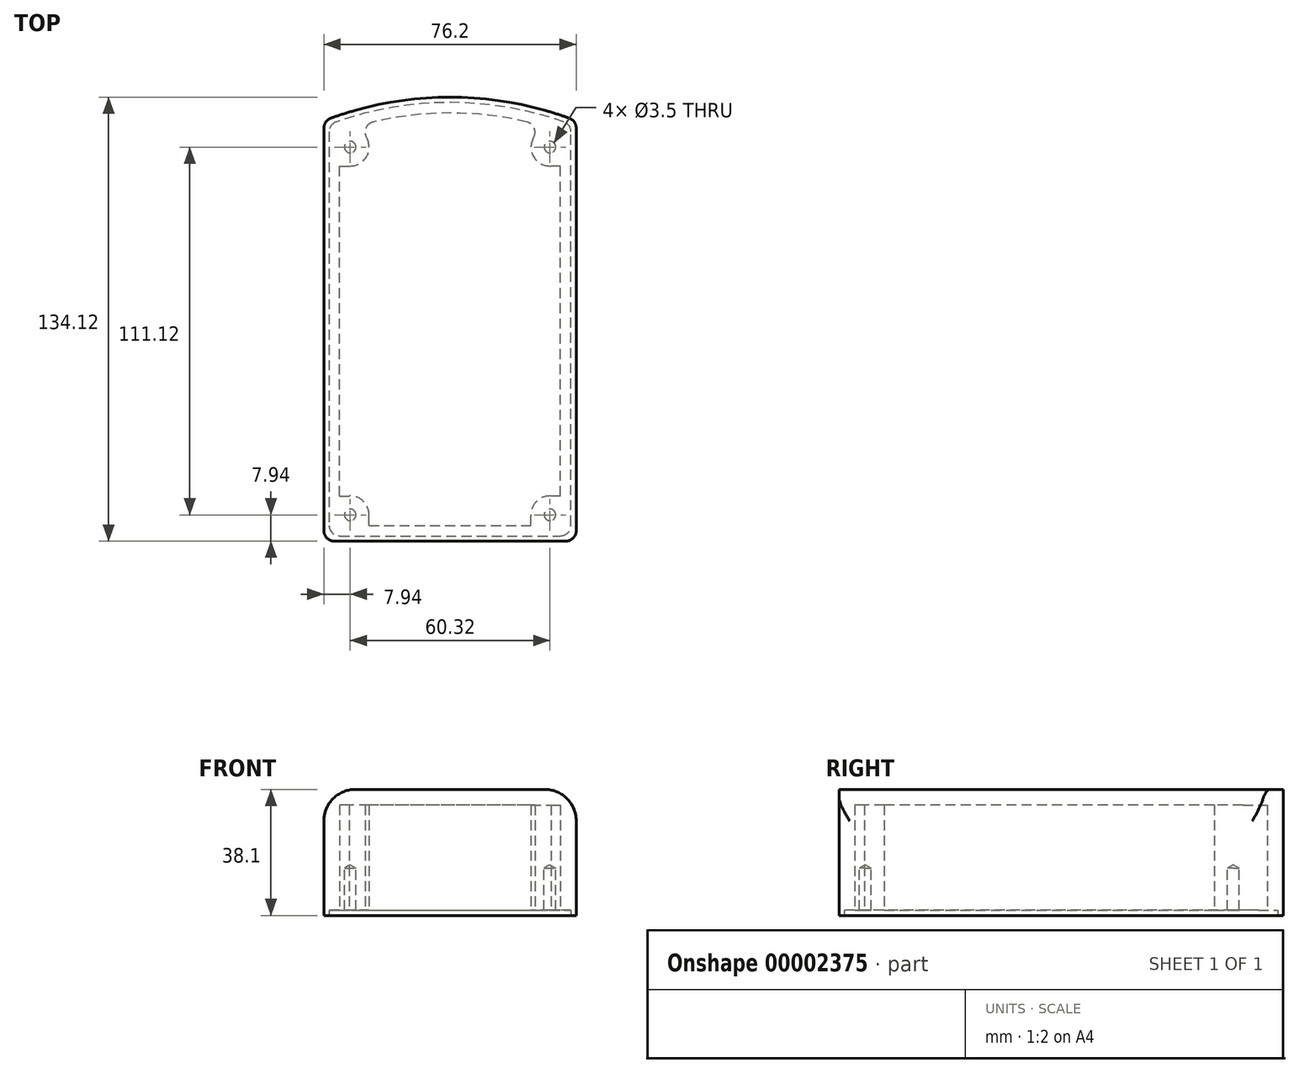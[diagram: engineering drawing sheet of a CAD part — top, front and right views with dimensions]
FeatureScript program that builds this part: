
annotation { "Feature Type Name" : "Feature", "Feature Type Description" : "" }
export const myFeature = defineFeature(function(context is Context, id is Id, definition is map)
    precondition{}
    {
        {
            var Q0;
            Q0=qCreatedBy(makeId("Top.planeOp"),FACE);
            var sketch = newSketch(context, id + "F0", { "sketchPlane" : qUnion([Q0])});
            skLineSegment(sketch, "E0.rect.bottom", {"start": v(38.1, 63.5) * mm, "end": v(-38.1, 63.5) * mm, "construction": true});
            skLineSegment(sketch, "E0.rect.top", {"start": v(38.1, -63.5) * mm, "end": v(-38.1, -63.5) * mm});
            skLineSegment(sketch, "E0.rect.left", {"start": v(38.1, 63.5) * mm, "end": v(38.1, -63.5) * mm});
            skLineSegment(sketch, "E0.rect.right", {"start": v(-38.1, 63.5) * mm, "end": v(-38.1, -63.5) * mm});
            skPoint(sketch, "E0.rect.middle", {"position": v(0, 0) * mm});
            skArc(sketch, "E1", {"start": v(38.1, 63.5) * mm, "mid": v(0, 70.62) * mm, "end": v(-38.1, 63.5) * mm});
            skSolve(sketch);
        }
        {
            var Q0;
            Q0 = qSketchRegion(id + "F0", true);
            extrude(context, id + "F1", {"entities" : qUnion([Q0]), "depth" : 38.1 * mm});
        }
        {
            var Q0;
            Q0=makeQuery(id+"F1.opExtrude","CAP_FACE",FACE,{"disambiguationData":[OSD([sQuery(id+"F0.wireOp",EDGE,"E0.rect.top"),sQuery(id+"F0.wireOp",EDGE,"E0.rect.left"),sQuery(id+"F0.wireOp",EDGE,"E0.rect.right"),sQuery(id+"F0.wireOp",EDGE,"E1")])],"isStart":true});
            shell(context, id + "F2", {"entities" : qUnion([Q0]), "thickness" : 4.76 * mm});
        }
        {
            var Q0;
            Q0=qCreatedBy(makeId("Top.planeOp"),FACE);
            var sketch = newSketch(context, id + "F3", { "sketchPlane" : qUnion([Q0])});
            skLineSegment(sketch, "E2.rect.bottom", {"start": v(30.16, -55.56) * mm, "end": v(-30.16, -55.56) * mm, "construction": true});
            skLineSegment(sketch, "E2.rect.top", {"start": v(30.16, 55.56) * mm, "end": v(-30.16, 55.56) * mm, "construction": true});
            skLineSegment(sketch, "E2.rect.left", {"start": v(30.16, -55.56) * mm, "end": v(30.16, 55.56) * mm, "construction": true});
            skLineSegment(sketch, "E2.rect.right", {"start": v(-30.16, -55.56) * mm, "end": v(-30.16, 55.56) * mm, "construction": true});
            skPoint(sketch, "E2.rect.middle", {"position": v(0, 0) * mm});
            skCircle(sketch, "E3", {"center": v(-30.16, -55.56) * mm, "radius": 5.72 * mm});
            skCircle(sketch, "E4", {"center": v(30.16, -55.56) * mm, "radius": 5.72 * mm});
            skCircle(sketch, "E5", {"center": v(30.16, 55.56) * mm, "radius": 5.72 * mm});
            skCircle(sketch, "E6", {"center": v(-30.16, 55.56) * mm, "radius": 5.72 * mm});
            skLineSegment(sketch, "E7", {"start": v(-30.16, 49.85) * mm, "end": v(-33.34, 49.85) * mm});
            skLineSegment(sketch, "E8", {"start": v(-24.45, 55.56) * mm, "end": v(-24.45, 62.84) * mm});
            skArc(sketch, "E9.0", {"start": v(33.34, 60.18) * mm, "mid": v(0, 65.85) * mm, "end": v(-33.34, 60.18) * mm});
            skLineSegment(sketch, "E9.1", {"start": v(-33.34, 60.18) * mm, "end": v(-33.34, -58.74) * mm});
            skLineSegment(sketch, "E10", {"start": v(24.45, 55.56) * mm, "end": v(24.45, 62.84) * mm});
            skLineSegment(sketch, "E11.0", {"start": v(33.34, 60.18) * mm, "end": v(33.34, -58.74) * mm});
            skLineSegment(sketch, "E12", {"start": v(30.16, 49.85) * mm, "end": v(33.34, 49.85) * mm});
            skLineSegment(sketch, "E13.0", {"start": v(33.34, -58.74) * mm, "end": v(-33.34, -58.74) * mm});
            skLineSegment(sketch, "E14", {"start": v(-24.45, -55.56) * mm, "end": v(-24.45, -58.74) * mm});
            skLineSegment(sketch, "E15", {"start": v(-30.16, -49.85) * mm, "end": v(-33.34, -49.85) * mm});
            skLineSegment(sketch, "E16", {"start": v(24.45, -55.56) * mm, "end": v(24.45, -58.74) * mm});
            skLineSegment(sketch, "E17", {"start": v(30.16, -49.85) * mm, "end": v(33.34, -49.85) * mm});
            skSolve(sketch);
        }
        {
            var Q0;
            {var subQ0=sQuery(id+"F3.wireOp",EDGE,"E15");Q0=makeQuery(id+"F3.imprint","IMPRINT",FACE,{"disambiguationData":[TD([[makeQuery(id+"F3.imprint","IMPRINT",EDGE,{"derivedFrom":subQ0}),1.0]])]});}
            var Q1;
            {var subQ1=sQuery(id+"F3.wireOp",EDGE,"E3");var subQ6=makeQuery(id+"F3.imprint","INTERSECT",VERTEX,{"derivedFrom":[subQ1,sQuery(id+"F3.wireOp",EDGE,"E14")]});Q1=makeQuery(id+"F3.imprint","IMPRINT",FACE,{"disambiguationData":[TD([[makeQuery(id+"F3.imprint","IMPRINT",EDGE,{"disambiguationData":[TD([[subQ6,-1.0]])],"derivedFrom":subQ1}),1.0]])]});}
            var Q2;
            {var subQ0=sQuery(id+"F3.wireOp",EDGE,"E14");Q2=makeQuery(id+"F3.imprint","IMPRINT",FACE,{"disambiguationData":[TD([[makeQuery(id+"F3.imprint","IMPRINT",EDGE,{"derivedFrom":subQ0}),-1.0]])]});}
            var Q3;
            {var subQ0=sQuery(id+"F3.wireOp",EDGE,"E16");Q3=makeQuery(id+"F3.imprint","IMPRINT",FACE,{"disambiguationData":[TD([[makeQuery(id+"F3.imprint","IMPRINT",EDGE,{"derivedFrom":subQ0}),1.0]])]});}
            var Q4;
            {var subQ1=sQuery(id+"F3.wireOp",EDGE,"E4");var subQ7=makeQuery(id+"F3.imprint","INTERSECT",VERTEX,{"derivedFrom":[subQ1,sQuery(id+"F3.wireOp",EDGE,"E17")]});Q4=makeQuery(id+"F3.imprint","IMPRINT",FACE,{"disambiguationData":[TD([[makeQuery(id+"F3.imprint","IMPRINT",EDGE,{"disambiguationData":[TD([[subQ7,1.0]])],"derivedFrom":subQ1}),1.0]])]});}
            var Q5;
            {var subQ0=sQuery(id+"F3.wireOp",EDGE,"E17");Q5=makeQuery(id+"F3.imprint","IMPRINT",FACE,{"disambiguationData":[TD([[makeQuery(id+"F3.imprint","IMPRINT",EDGE,{"derivedFrom":subQ0}),-1.0]])]});}
            var Q6;
            {var subQ3=sQuery(id+"F3.wireOp",EDGE,"E7");Q6=makeQuery(id+"F3.imprint","IMPRINT",FACE,{"disambiguationData":[TD([[makeQuery(id+"F3.imprint","IMPRINT",EDGE,{"derivedFrom":subQ3}),-1.0]])]});}
            var Q7;
            {var subQ1=sQuery(id+"F3.wireOp",EDGE,"E6");var subQ6=makeQuery(id+"F3.imprint","INTERSECT",VERTEX,{"derivedFrom":[subQ1,sQuery(id+"F3.wireOp",EDGE,"E8")]});Q7=makeQuery(id+"F3.imprint","IMPRINT",FACE,{"disambiguationData":[TD([[makeQuery(id+"F3.imprint","IMPRINT",EDGE,{"disambiguationData":[TD([[subQ6,-1.0]])],"derivedFrom":subQ1}),1.0]])]});}
            var Q8;
            {var subQ3=sQuery(id+"F3.wireOp",EDGE,"E8");Q8=makeQuery(id+"F3.imprint","IMPRINT",FACE,{"disambiguationData":[TD([[makeQuery(id+"F3.imprint","IMPRINT",EDGE,{"derivedFrom":subQ3}),1.0]])]});}
            var Q9;
            {var subQ0=sQuery(id+"F3.wireOp",EDGE,"E10");Q9=makeQuery(id+"F3.imprint","IMPRINT",FACE,{"disambiguationData":[TD([[makeQuery(id+"F3.imprint","IMPRINT",EDGE,{"derivedFrom":subQ0}),-1.0]])]});}
            var Q10;
            {var subQ1=sQuery(id+"F3.wireOp",EDGE,"E5");var subQ7=makeQuery(id+"F3.imprint","INTERSECT",VERTEX,{"derivedFrom":[subQ1,sQuery(id+"F3.wireOp",EDGE,"E10")]});Q10=makeQuery(id+"F3.imprint","IMPRINT",FACE,{"disambiguationData":[TD([[makeQuery(id+"F3.imprint","IMPRINT",EDGE,{"disambiguationData":[TD([[subQ7,1.0]])],"derivedFrom":subQ1}),1.0]])]});}
            var Q11;
            {var subQ0=sQuery(id+"F3.wireOp",EDGE,"E12");Q11=makeQuery(id+"F3.imprint","IMPRINT",FACE,{"disambiguationData":[TD([[makeQuery(id+"F3.imprint","IMPRINT",EDGE,{"derivedFrom":subQ0}),1.0]])]});}
            var Q12;
            Q12=makeQuery(id+"F2.opShell","OFFSET_FACE",FACE,{"disambiguationData":[OSD([sQuery(id+"F0.wireOp",EDGE,"E0.rect.top"),sQuery(id+"F0.wireOp",EDGE,"E0.rect.left"),sQuery(id+"F0.wireOp",EDGE,"E0.rect.right"),sQuery(id+"F0.wireOp",EDGE,"E1")])]});
            extrude(context, id + "F4", {"entities" : qUnion([Q0, Q1, Q2, Q3, Q4, Q5, Q6, Q7, Q8, Q9, Q10, Q11]), "operationType" : NewBodyOperationType.ADD, "endBound" : BoundingType.UP_TO_SURFACE, "endBoundEntityFace" : qUnion([Q12]), "depth" : 25.4 * mm});
        }
        {
            var Q0;
            Q0=makeQuery(id+"F1.opExtrude","SWEPT_EDGE",EDGE,{"disambiguationData":[OSD([sQuery(id+"F0.wireOp",EDGE,"E0.rect.top"),sQuery(id+"F0.wireOp",EDGE,"E0.rect.left")])]});
            var Q1;
            Q1=makeQuery(id+"F1.opExtrude","SWEPT_EDGE",EDGE,{"disambiguationData":[OSD([sQuery(id+"F0.wireOp",EDGE,"E0.rect.top"),sQuery(id+"F0.wireOp",EDGE,"E0.rect.right")])]});
            var Q2;
            Q2=makeQuery(id+"F1.opExtrude","SWEPT_EDGE",EDGE,{"disambiguationData":[OSD([sQuery(id+"F0.wireOp",EDGE,"E0.rect.bottom"),sQuery(id+"F0.wireOp",EDGE,"E0.rect.left")])]});
            var Q3;
            Q3=makeQuery(id+"F1.opExtrude","SWEPT_EDGE",EDGE,{"disambiguationData":[OSD([sQuery(id+"F0.wireOp",EDGE,"E0.rect.bottom"),sQuery(id+"F0.wireOp",EDGE,"E0.rect.right")])]});
            fillet(context, id + "F5", {"entities" : qUnion([Q0, Q1, Q2, Q3]), "radius" : 3.17 * mm, "tangentPropagation" : true, "allowEdgeOverflow" : false});
        }
        {
            var Q0;
            Q0=makeQuery(id+"F1.opExtrude","CAP_EDGE",EDGE,{"disambiguationData":[OSD([sQuery(id+"F0.wireOp",EDGE,"E0.rect.right")])],"isStart":false});
            var Q1;
            Q1=makeQuery(id+"F1.opExtrude","CAP_EDGE",EDGE,{"disambiguationData":[OSD([sQuery(id+"F0.wireOp",EDGE,"E0.rect.left")])],"isStart":false});
            fillet(context, id + "F6", {"entities" : qUnion([Q0, Q1]), "radius" : 9.52 * mm, "allowEdgeOverflow" : false});
        }
        {
            var Q0;
            Q0=makeQuery(id+"F4.boolean.opBoolean","INTERSECT",EDGE,{"derivedFrom":[makeQuery(id+"F2.opShell","OFFSET_FACE",FACE,{"disambiguationData":[OSD([sQuery(id+"F0.wireOp",EDGE,"E0.rect.right")])]}),makeQuery(id+"F4.opExtrude","SWEPT_FACE",FACE,{"disambiguationData":[OSD([sQuery(id+"F3.wireOp",EDGE,"E3")])]})]});
            var Q1;
            Q1=makeQuery(id+"F4.boolean.opBoolean","INTERSECT",EDGE,{"derivedFrom":[makeQuery(id+"F2.opShell","OFFSET_FACE",FACE,{"disambiguationData":[OSD([sQuery(id+"F0.wireOp",EDGE,"E0.rect.top")])]}),makeQuery(id+"F4.opExtrude","SWEPT_FACE",FACE,{"disambiguationData":[OSD([sQuery(id+"F3.wireOp",EDGE,"E3")])]})]});
            var Q2;
            Q2=makeQuery(id+"F4.boolean.opBoolean","INTERSECT",EDGE,{"derivedFrom":[makeQuery(id+"F2.opShell","OFFSET_FACE",FACE,{"disambiguationData":[OSD([sQuery(id+"F0.wireOp",EDGE,"E0.rect.top")])]}),makeQuery(id+"F4.opExtrude","SWEPT_FACE",FACE,{"disambiguationData":[OSD([sQuery(id+"F3.wireOp",EDGE,"E4")])]})]});
            var Q3;
            Q3=makeQuery(id+"F4.boolean.opBoolean","INTERSECT",EDGE,{"derivedFrom":[makeQuery(id+"F2.opShell","OFFSET_FACE",FACE,{"disambiguationData":[OSD([sQuery(id+"F0.wireOp",EDGE,"E0.rect.left")])]}),makeQuery(id+"F4.opExtrude","SWEPT_FACE",FACE,{"disambiguationData":[OSD([sQuery(id+"F3.wireOp",EDGE,"E4")])]})]});
            var Q4;
            Q4=makeQuery(id+"F4.boolean.opBoolean","INTERSECT",EDGE,{"derivedFrom":[makeQuery(id+"F2.opShell","OFFSET_FACE",FACE,{"disambiguationData":[OSD([sQuery(id+"F0.wireOp",EDGE,"E1")])]}),makeQuery(id+"F4.opExtrude","SWEPT_FACE",FACE,{"disambiguationData":[OSD([sQuery(id+"F3.wireOp",EDGE,"E6")])]})]});
            var Q5;
            Q5=makeQuery(id+"F4.boolean.opBoolean","INTERSECT",EDGE,{"derivedFrom":[makeQuery(id+"F2.opShell","OFFSET_FACE",FACE,{"disambiguationData":[OSD([sQuery(id+"F0.wireOp",EDGE,"E0.rect.right")])]}),makeQuery(id+"F4.opExtrude","SWEPT_FACE",FACE,{"disambiguationData":[OSD([sQuery(id+"F3.wireOp",EDGE,"E6")])]})]});
            var Q6;
            Q6=makeQuery(id+"F4.boolean.opBoolean","INTERSECT",EDGE,{"derivedFrom":[makeQuery(id+"F2.opShell","OFFSET_FACE",FACE,{"disambiguationData":[OSD([sQuery(id+"F0.wireOp",EDGE,"E1")])]}),makeQuery(id+"F4.opExtrude","SWEPT_FACE",FACE,{"disambiguationData":[OSD([sQuery(id+"F3.wireOp",EDGE,"E5")])]})]});
            var Q7;
            Q7=makeQuery(id+"F4.boolean.opBoolean","INTERSECT",EDGE,{"derivedFrom":[makeQuery(id+"F2.opShell","OFFSET_FACE",FACE,{"disambiguationData":[OSD([sQuery(id+"F0.wireOp",EDGE,"E0.rect.left")])]}),makeQuery(id+"F4.opExtrude","SWEPT_FACE",FACE,{"disambiguationData":[OSD([sQuery(id+"F3.wireOp",EDGE,"E5")])]})]});
            var Q8;
            Q8=makeQuery(id+"F4.opExtrude","SWEPT_EDGE",EDGE,{"disambiguationData":[OSD([sQuery(id+"F3.wireOp",EDGE,"E8"),sQuery(id+"F3.wireOp",EDGE,"E9.0")])]});
            var Q9;
            Q9=makeQuery(id+"F4.opExtrude","SWEPT_EDGE",EDGE,{"disambiguationData":[OSD([sQuery(id+"F3.wireOp",EDGE,"E7"),sQuery(id+"F3.wireOp",EDGE,"E9.1")])]});
            var Q10;
            Q10=makeQuery(id+"F4.opExtrude","SWEPT_EDGE",EDGE,{"disambiguationData":[OSD([sQuery(id+"F3.wireOp",EDGE,"E9.0"),sQuery(id+"F3.wireOp",EDGE,"E10")])]});
            var Q11;
            Q11=makeQuery(id+"F4.opExtrude","SWEPT_EDGE",EDGE,{"disambiguationData":[OSD([sQuery(id+"F3.wireOp",EDGE,"E11.0"),sQuery(id+"F3.wireOp",EDGE,"E12")])]});
            var Q12;
            Q12=makeQuery(id+"F4.opExtrude","SWEPT_EDGE",EDGE,{"disambiguationData":[OSD([sQuery(id+"F3.wireOp",EDGE,"E9.1"),sQuery(id+"F3.wireOp",EDGE,"E15")])]});
            var Q13;
            Q13=makeQuery(id+"F4.opExtrude","SWEPT_EDGE",EDGE,{"disambiguationData":[OSD([sQuery(id+"F3.wireOp",EDGE,"E13.0"),sQuery(id+"F3.wireOp",EDGE,"E14")])]});
            var Q14;
            Q14=makeQuery(id+"F4.opExtrude","SWEPT_EDGE",EDGE,{"disambiguationData":[OSD([sQuery(id+"F3.wireOp",EDGE,"E13.0"),sQuery(id+"F3.wireOp",EDGE,"E16")])]});
            var Q15;
            Q15=makeQuery(id+"F4.opExtrude","SWEPT_EDGE",EDGE,{"disambiguationData":[OSD([sQuery(id+"F3.wireOp",EDGE,"E11.0"),sQuery(id+"F3.wireOp",EDGE,"E17")])]});
            fillet(context, id + "F7", {"entities" : qUnion([Q0, Q1, Q2, Q3, Q4, Q5, Q6, Q7, Q8, Q9, Q10, Q11, Q12, Q13, Q14, Q15]), "radius" : 3.17 * mm, "tangentPropagation" : true, "allowEdgeOverflow" : false});
        }
        {
            var Q0;
            Q0=makeQuery(id+"F4.boolean.opBoolean","MERGE",FACE,{"derivedFrom":[makeQuery(id+"F1.opExtrude","CAP_FACE",FACE,{"disambiguationData":[OSD([sQuery(id+"F0.wireOp",EDGE,"E0.rect.top"),sQuery(id+"F0.wireOp",EDGE,"E0.rect.left"),sQuery(id+"F0.wireOp",EDGE,"E0.rect.right"),sQuery(id+"F0.wireOp",EDGE,"E1")])],"isStart":true}),makeQuery(id+"F4.opExtrude","CAP_FACE",FACE,{"disambiguationData":[OSD([sQuery(id+"F3.wireOp",EDGE,"E3")])],"isStart":true}),makeQuery(id+"F4.opExtrude","CAP_FACE",FACE,{"disambiguationData":[OSD([sQuery(id+"F3.wireOp",EDGE,"E4")])],"isStart":true}),makeQuery(id+"F4.opExtrude","CAP_FACE",FACE,{"disambiguationData":[OSD([sQuery(id+"F3.wireOp",EDGE,"E5")])],"isStart":true}),makeQuery(id+"F4.opExtrude","CAP_FACE",FACE,{"disambiguationData":[OSD([sQuery(id+"F3.wireOp",EDGE,"E6")])],"isStart":true})]});
            var sketch = newSketch(context, id + "F8", { "sketchPlane" : qUnion([Q0])});
            skLineSegment(sketch, "E18.0", {"start": v(-36.51, 61.91) * mm, "end": v(36.51, 61.91) * mm});
            skLineSegment(sketch, "E18.1", {"start": v(-36.51, -62.4) * mm, "end": v(-36.51, 61.91) * mm});
            skArc(sketch, "E18.2", {"start": v(36.51, -62.4) * mm, "mid": v(0, -69.03) * mm, "end": v(-36.51, -62.4) * mm});
            skLineSegment(sketch, "E18.3", {"start": v(36.51, 61.91) * mm, "end": v(36.51, -62.4) * mm});
            skSolve(sketch);
        }
        {
            var Q0;
            Q0 = qSketchRegion(id + "F8", true);
            extrude(context, id + "F9", {"entities" : qUnion([Q0]), "operationType" : NewBodyOperationType.REMOVE, "oppositeDirection" : true, "depth" : 1.59 * mm});
        }
        {
            var Q0;
            Q0=makeQuery(id+"F9.boolean.opBoolean","COPY",EDGE,{"derivedFrom":makeQuery(id+"F9.opExtrude","SWEPT_EDGE",EDGE,{"disambiguationData":[OSD([sQuery(id+"F8.wireOp",EDGE,"E18.0"),sQuery(id+"F8.wireOp",EDGE,"E18.1")])]})});
            var Q1;
            Q1=makeQuery(id+"F9.boolean.opBoolean","COPY",EDGE,{"derivedFrom":makeQuery(id+"F9.opExtrude","SWEPT_EDGE",EDGE,{"disambiguationData":[OSD([sQuery(id+"F8.wireOp",EDGE,"E18.0"),sQuery(id+"F8.wireOp",EDGE,"E18.3")])]})});
            var Q2;
            Q2=makeQuery(id+"F9.boolean.opBoolean","COPY",EDGE,{"derivedFrom":makeQuery(id+"F9.opExtrude","SWEPT_EDGE",EDGE,{"disambiguationData":[OSD([sQuery(id+"F8.wireOp",EDGE,"E18.1"),sQuery(id+"F8.wireOp",EDGE,"E18.2")])]})});
            var Q3;
            Q3=makeQuery(id+"F9.boolean.opBoolean","COPY",EDGE,{"derivedFrom":makeQuery(id+"F9.opExtrude","SWEPT_EDGE",EDGE,{"disambiguationData":[OSD([sQuery(id+"F8.wireOp",EDGE,"E18.2"),sQuery(id+"F8.wireOp",EDGE,"E18.3")])]})});
            fillet(context, id + "F10", {"entities" : qUnion([Q0, Q1, Q2, Q3]), "radius" : 3.17 * mm, "tangentPropagation" : true, "allowEdgeOverflow" : false});
        }
        {
            var Q0;
            Q0=makeQuery(id+"F9.boolean.opBoolean","COPY",FACE,{"derivedFrom":makeQuery(id+"F9.opExtrude","CAP_FACE",FACE,{"disambiguationData":[OSD([sQuery(id+"F8.wireOp",EDGE,"E18.0"),sQuery(id+"F8.wireOp",EDGE,"E18.1"),sQuery(id+"F8.wireOp",EDGE,"E18.2"),sQuery(id+"F8.wireOp",EDGE,"E18.3")])],"isStart":false})});
            var sketch = newSketch(context, id + "F11", { "sketchPlane" : qUnion([Q0])});
            skPoint(sketch, "E19", {"position": v(-30.16, 55.56) * mm});
            skPoint(sketch, "E20", {"position": v(30.16, 55.56) * mm});
            skPoint(sketch, "E21", {"position": v(-30.16, -55.56) * mm});
            skPoint(sketch, "E22", {"position": v(30.16, -55.56) * mm});
            skSolve(sketch);
        }
        {
            var Q0;
            Q0=sQuery(id+"F11.wireOp",VERTEX,"E21");
            var Q1;
            Q1=sQuery(id+"F11.wireOp",VERTEX,"E22");
            var Q2;
            Q2=sQuery(id+"F11.wireOp",VERTEX,"E19");
            var Q3;
            Q3=sQuery(id+"F11.wireOp",VERTEX,"E20");
            var Q4;
            Q4=makeQuery(id+"F1.opExtrude","SWEPT_BODY",BODY,{"disambiguationData":[OSD([sQuery(id+"F0.wireOp",EDGE,"E0.rect.top"),sQuery(id+"F0.wireOp",EDGE,"E0.rect.left"),sQuery(id+"F0.wireOp",EDGE,"E0.rect.right"),sQuery(id+"F0.wireOp",EDGE,"E1")])]});
            hole(context, id + "F12", {"style" : HoleStyle.SIMPLE, "holeDiameter" : 3.5 * mm, "endStyle" : HoleEndStyle.BLIND, "holeDepth" : 12.7 * mm, "locations" : qUnion([Q0, Q1, Q2, Q3]), "scope" : qUnion([Q4])});
        }
    });
